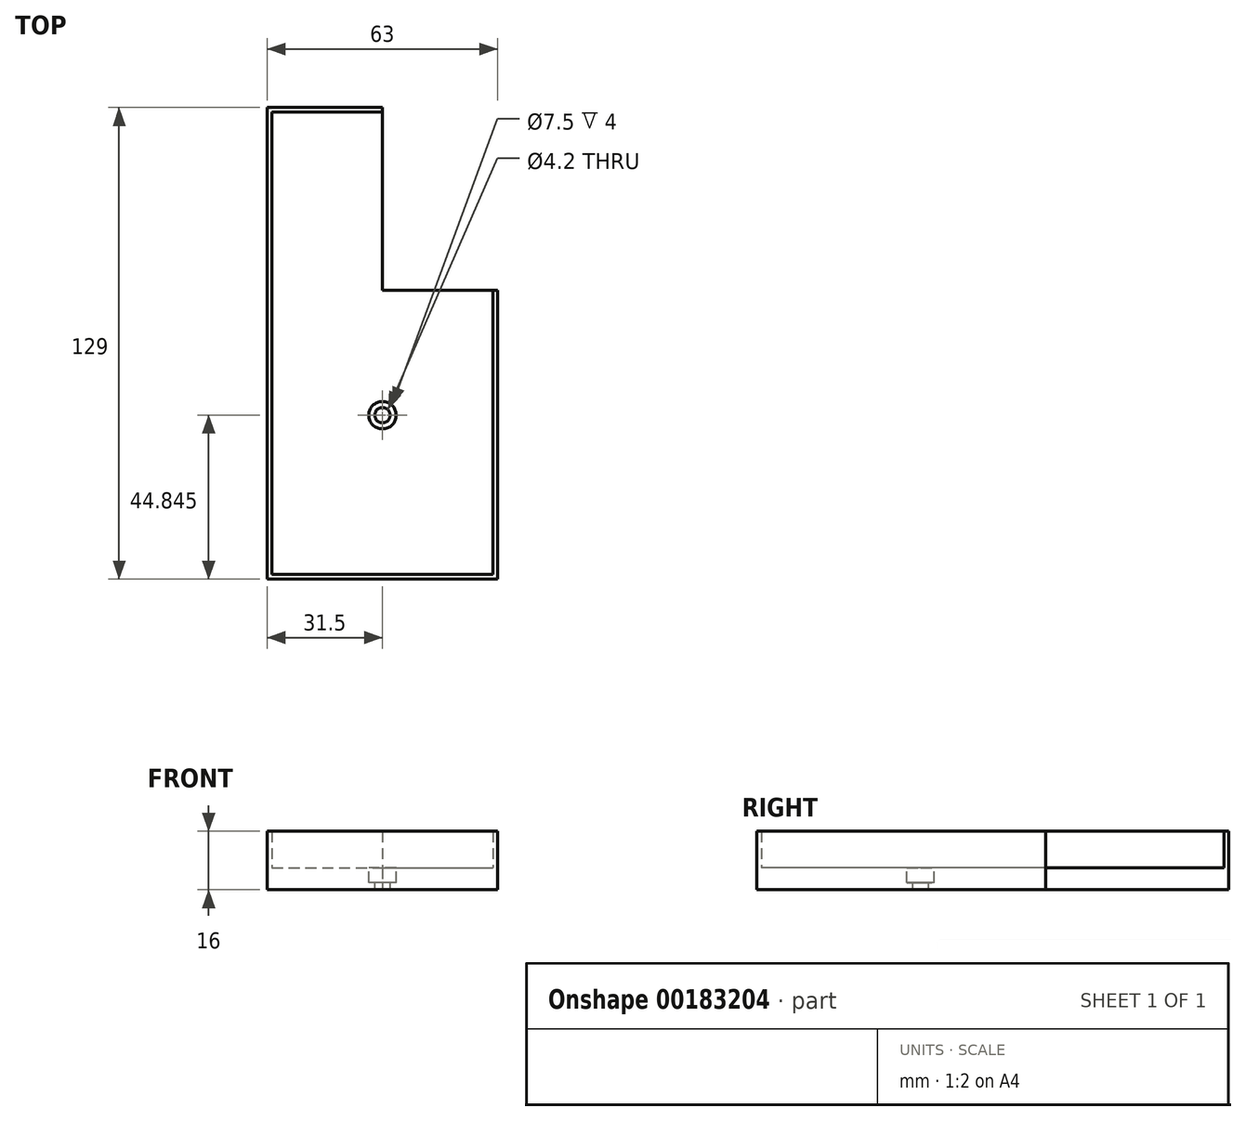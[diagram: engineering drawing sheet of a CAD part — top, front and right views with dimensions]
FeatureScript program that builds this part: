
annotation { "Feature Type Name" : "Feature", "Feature Type Description" : "" }
export const myFeature = defineFeature(function(context is Context, id is Id, definition is map)
    precondition{}
    {
        {
            var Q0;
            Q0=qCreatedBy(makeId("Top.planeOp"),FACE);
            var sketch = newSketch(context, id + "F0", { "sketchPlane" : qUnion([Q0])});
            skLineSegment(sketch, "E0.bottom", {"start": v(31.5, -64.5) * mm, "end": v(-31.5, -64.5) * mm});
            skLineSegment(sketch, "E0.top", {"start": v(31.5, 64.5) * mm, "end": v(-31.5, 64.5) * mm});
            skLineSegment(sketch, "E0.left", {"start": v(31.5, -64.5) * mm, "end": v(31.5, 64.5) * mm});
            skLineSegment(sketch, "E0.right", {"start": v(-31.5, -64.5) * mm, "end": v(-31.5, 64.5) * mm});
            skPoint(sketch, "E0.middle", {"position": v(0, 0) * mm});
            skLineSegment(sketch, "E1.bottom", {"start": v(0, 64.5) * mm, "end": v(31.5, 64.5) * mm});
            skLineSegment(sketch, "E1.top", {"start": v(0, 14.5) * mm, "end": v(31.5, 14.5) * mm});
            skLineSegment(sketch, "E1.left", {"start": v(0, 64.5) * mm, "end": v(0, 14.5) * mm});
            skLineSegment(sketch, "E1.right", {"start": v(31.5, 64.5) * mm, "end": v(31.5, 14.5) * mm});
            skSolve(sketch);
        }
        {
            var Q0;
            Q0=makeQuery(id+"F0.imprint","IMPRINT",FACE,{"disambiguationData":[TD([[makeQuery(id+"F0.imprint","IMPRINT",EDGE,{"derivedFrom":sQuery(id+"F0.wireOp",EDGE,"E0.bottom")}),-1.0]])]});
            extrude(context, id + "F1", {"entities" : qUnion([Q0]), "depth" : 6 * mm});
        }
        {
            var Q0;
            Q0=makeQuery(id+"F1.opExtrude","CAP_FACE",FACE,{"disambiguationData":[OSD([sQuery(id+"F0.wireOp",EDGE,"E0.bottom"),sQuery(id+"F0.wireOp",EDGE,"E0.top"),sQuery(id+"F0.wireOp",EDGE,"E0.left"),sQuery(id+"F0.wireOp",EDGE,"E0.right"),sQuery(id+"F0.wireOp",EDGE,"UvZCbneQ-QbZr-ikUp-hfei-MtuENPK6z4fk.top"),sQuery(id+"F0.wireOp",EDGE,"UvZCbneQ-QbZr-ikUp-hfei-MtuENPK6z4fk.right")])],"isStart":false});
            var sketch = newSketch(context, id + "F2", { "sketchPlane" : qUnion([Q0])});
            skLineSegment(sketch, "E2.left", {"start": v(-31.5, 64.5) * mm, "end": v(-31.5, 63.25) * mm});
            skLineSegment(sketch, "E2.right", {"start": v(31.5, 64.5) * mm, "end": v(31.5, 63.25) * mm});
            skLineSegment(sketch, "E3.left", {"start": v(-31.5, -63.25) * mm, "end": v(-31.5, -64.5) * mm});
            skLineSegment(sketch, "E3.right", {"start": v(31.5, -63.25) * mm, "end": v(31.5, -64.5) * mm});
            skLineSegment(sketch, "E4.bottom", {"start": v(30.25, 63.25) * mm, "end": v(31.5, 63.25) * mm});
            skLineSegment(sketch, "E4.top", {"start": v(30.25, -63.25) * mm, "end": v(31.5, -63.25) * mm});
            skLineSegment(sketch, "E5.bottom", {"start": v(-31.5, -64.5) * mm, "end": v(-30.25, -64.5) * mm});
            skLineSegment(sketch, "E5.top", {"start": v(-31.5, -63.25) * mm, "end": v(-30.25, -63.25) * mm});
            skLineSegment(sketch, "E5.right", {"start": v(-30.25, -63.25) * mm, "end": v(-30.25, -64.5) * mm});
            skLineSegment(sketch, "E6.bottom", {"start": v(-31.5, 63.25) * mm, "end": v(-31.5, 63.25) * mm});
            skLineSegment(sketch, "E6.top", {"start": v(-31.5, -63.25) * mm, "end": v(-31.5, -63.25) * mm});
            skLineSegment(sketch, "E6.left", {"start": v(-31.5, 63.25) * mm, "end": v(-31.5, -63.25) * mm});
            skLineSegment(sketch, "E7.bottom", {"start": v(-31.5, 63.25) * mm, "end": v(-29, 63.25) * mm});
            skPoint(sketch, "E8.oppositeSnap0", {"position": v(-30.25, 63.25) * mm});
            skLineSegment(sketch, "E8.bottom", {"start": v(-31.5, 63.25) * mm, "end": v(-30.25, 63.25) * mm});
            skLineSegment(sketch, "E8.right", {"start": v(-30.25, 63.25) * mm, "end": v(-30.25, -63.25) * mm});
            skLineSegment(sketch, "E9.left", {"start": v(31.5, -63.25) * mm, "end": v(31.5, -63.25) * mm});
            skLineSegment(sketch, "E9.right", {"start": v(-30.25, -63.25) * mm, "end": v(-30.25, -63.25) * mm});
            skLineSegment(sketch, "E10.bottom", {"start": v(30.25, 14.5) * mm, "end": v(31.5, 14.5) * mm});
            skLineSegment(sketch, "E10.left", {"start": v(30.25, 14.5) * mm, "end": v(30.25, -63.25) * mm});
            skLineSegment(sketch, "E10.right", {"start": v(31.5, 14.5) * mm, "end": v(31.5, -63.25) * mm});
            skLineSegment(sketch, "E11.bottom", {"start": v(-31.5, 64.5) * mm, "end": v(0, 64.5) * mm});
            skLineSegment(sketch, "E11.top", {"start": v(-31.5, 63.25) * mm, "end": v(0, 63.25) * mm});
            skLineSegment(sketch, "E11.right", {"start": v(0, 64.5) * mm, "end": v(0, 63.25) * mm});
            skLineSegment(sketch, "E12.bottom", {"start": v(-30.25, -63.25) * mm, "end": v(31.5, -63.25) * mm});
            skLineSegment(sketch, "E12.top", {"start": v(-30.25, -64.5) * mm, "end": v(31.5, -64.5) * mm});
            skSolve(sketch);
        }
        {
            var Q0;
            Q0 = qSketchRegion(id + "F2", true);
            extrude(context, id + "F3", {"entities" : qUnion([Q0]), "operationType" : NewBodyOperationType.ADD, "depth" : 10 * mm});
        }
        {
            var Q0;
            Q0=makeQuery(id+"F1.opExtrude","CAP_FACE",FACE,{"disambiguationData":[OSD([sQuery(id+"F0.wireOp",EDGE,"E0.bottom"),sQuery(id+"F0.wireOp",EDGE,"E0.top"),sQuery(id+"F0.wireOp",EDGE,"E0.left"),sQuery(id+"F0.wireOp",EDGE,"E0.right"),sQuery(id+"F0.wireOp",EDGE,"UvZCbneQ-QbZr-ikUp-hfei-MtuENPK6z4fk.top"),sQuery(id+"F0.wireOp",EDGE,"UvZCbneQ-QbZr-ikUp-hfei-MtuENPK6z4fk.right")])],"isStart":false});
            var sketch = newSketch(context, id + "F4", { "sketchPlane" : qUnion([Q0])});
            skCircle(sketch, "E13", {"center": v(0, -19.65) * mm, "radius": 3.75 * mm});
            skSolve(sketch);
        }
        {
            var Q0;
            Q0 = qSketchRegion(id + "F4", true);
            extrude(context, id + "F5", {"entities" : qUnion([Q0]), "operationType" : NewBodyOperationType.REMOVE, "oppositeDirection" : true, "depth" : 4 * mm});
        }
        {
            var Q0;
            Q0=makeQuery(id+"F5.boolean.opBoolean","COPY",FACE,{"derivedFrom":makeQuery(id+"F5.opExtrude","CAP_FACE",FACE,{"disambiguationData":[OSD([sQuery(id+"F4.wireOp",EDGE,"E13")])],"isStart":false})});
            var sketch = newSketch(context, id + "F6", { "sketchPlane" : qUnion([Q0])});
            skCircle(sketch, "E14", {"center": v(0, -19.65) * mm, "radius": 2.1 * mm});
            skSolve(sketch);
        }
        {
            var Q0;
            Q0=makeQuery(id+"F6.imprint","IMPRINT",FACE,{"disambiguationData":[TD([[makeQuery(id+"F6.imprint","IMPRINT",EDGE,{"derivedFrom":sQuery(id+"F6.wireOp",EDGE,"E14")}),1.0]])]});
            extrude(context, id + "F7", {"entities" : qUnion([Q0]), "operationType" : NewBodyOperationType.REMOVE, "endBound" : BoundingType.UP_TO_NEXT, "oppositeDirection" : true, "depth" : 25 * mm});
        }
    });
